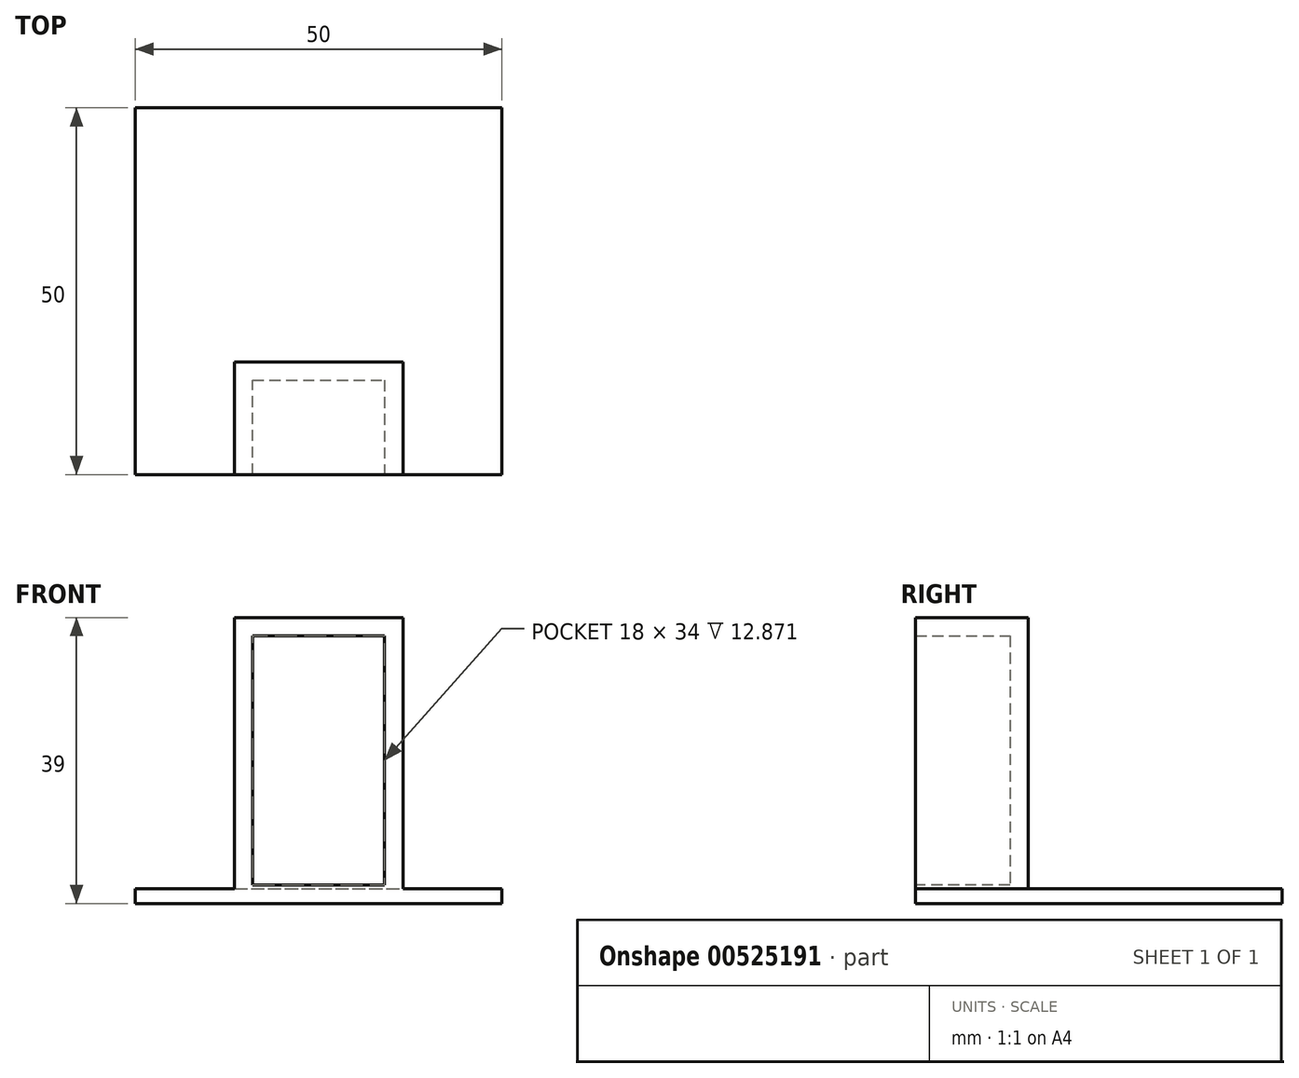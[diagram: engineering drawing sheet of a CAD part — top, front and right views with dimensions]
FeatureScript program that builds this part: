
annotation { "Feature Type Name" : "Feature", "Feature Type Description" : "" }
export const myFeature = defineFeature(function(context is Context, id is Id, definition is map)
    precondition{}
    {
        {
            var Q0;
            Q0=qCreatedBy(makeId("Top.planeOp"),FACE);
            var sketch = newSketch(context, id + "F0", { "sketchPlane" : qUnion([Q0])});
            skLineSegment(sketch, "E0.bottom", {"start": v(-25, 25) * mm, "end": v(25, 25) * mm});
            skLineSegment(sketch, "E0.top", {"start": v(-25, -25) * mm, "end": v(25, -25) * mm});
            skLineSegment(sketch, "E0.left", {"start": v(-25, 25) * mm, "end": v(-25, -25) * mm});
            skLineSegment(sketch, "E0.right", {"start": v(25, 25) * mm, "end": v(25, -25) * mm});
            skPoint(sketch, "E0.middle", {"position": v(0, 0) * mm});
            skLineSegment(sketch, "E1", {"start": v(-11.5, -25) * mm, "end": v(-11.5, -9.63) * mm});
            skLineSegment(sketch, "E2", {"start": v(-11.5, -9.63) * mm, "end": v(11.5, -9.63) * mm});
            skLineSegment(sketch, "E3", {"start": v(11.5, -9.63) * mm, "end": v(11.5, -25) * mm});
            skSolve(sketch);
        }
        {
            var Q0;
            {var subQ0=sQuery(id+"F0.wireOp",EDGE,"E1");Q0=makeQuery(id+"F0.imprint","IMPRINT",FACE,{"disambiguationData":[TD([[makeQuery(id+"F0.imprint","IMPRINT",EDGE,{"derivedFrom":subQ0}),-1.0]])]});}
            extrude(context, id + "F1", {"entities" : qUnion([Q0]), "depth" : 39 * mm, "offsetDistance" : 25 * mm});
        }
        {
            var Q0;
            Q0=makeQuery(id+"F0.imprint","IMPRINT",FACE,{"disambiguationData":[TD([[makeQuery(id+"F0.imprint","IMPRINT",EDGE,{"derivedFrom":sQuery(id+"F0.wireOp",EDGE,"E0.bottom")}),-1.0]])]});
            extrude(context, id + "F2", {"entities" : qUnion([Q0]), "operationType" : NewBodyOperationType.ADD, "depth" : 2 * mm, "offsetDistance" : 25 * mm});
        }
        {
            var Q0;
            {var subQ0=sQuery(id+"F0.wireOp",EDGE,"E0.top");Q0=makeQuery(id+"F2.boolean.opBoolean","MERGE",FACE,{"derivedFrom":[makeQuery(id+"F1.opExtrude","SWEPT_FACE",FACE,{"disambiguationData":[OSD([subQ0])]}),makeQuery(id+"F2.opExtrude","SWEPT_FACE",FACE,{"disambiguationData":[OSD([subQ0]),TDD([makeQuery(id+"F0.imprint","IMPRINT",EDGE,{"disambiguationData":[TD([[makeQuery(id+"F0.imprint","INTERSECT",VERTEX,{"derivedFrom":[subQ0,sQuery(id+"F0.wireOp",EDGE,"E0.left")]}),-1.0]])],"derivedFrom":subQ0})])]}),makeQuery(id+"F2.opExtrude","SWEPT_FACE",FACE,{"disambiguationData":[OSD([subQ0]),TDD([makeQuery(id+"F0.imprint","IMPRINT",EDGE,{"disambiguationData":[TD([[makeQuery(id+"F0.imprint","INTERSECT",VERTEX,{"derivedFrom":[subQ0,sQuery(id+"F0.wireOp",EDGE,"E0.right")]}),1.0]])],"derivedFrom":subQ0})])]})]});}
            shell(context, id + "F3", {"entities" : qUnion([Q0]), "thickness" : 2.5 * mm});
        }
    });
